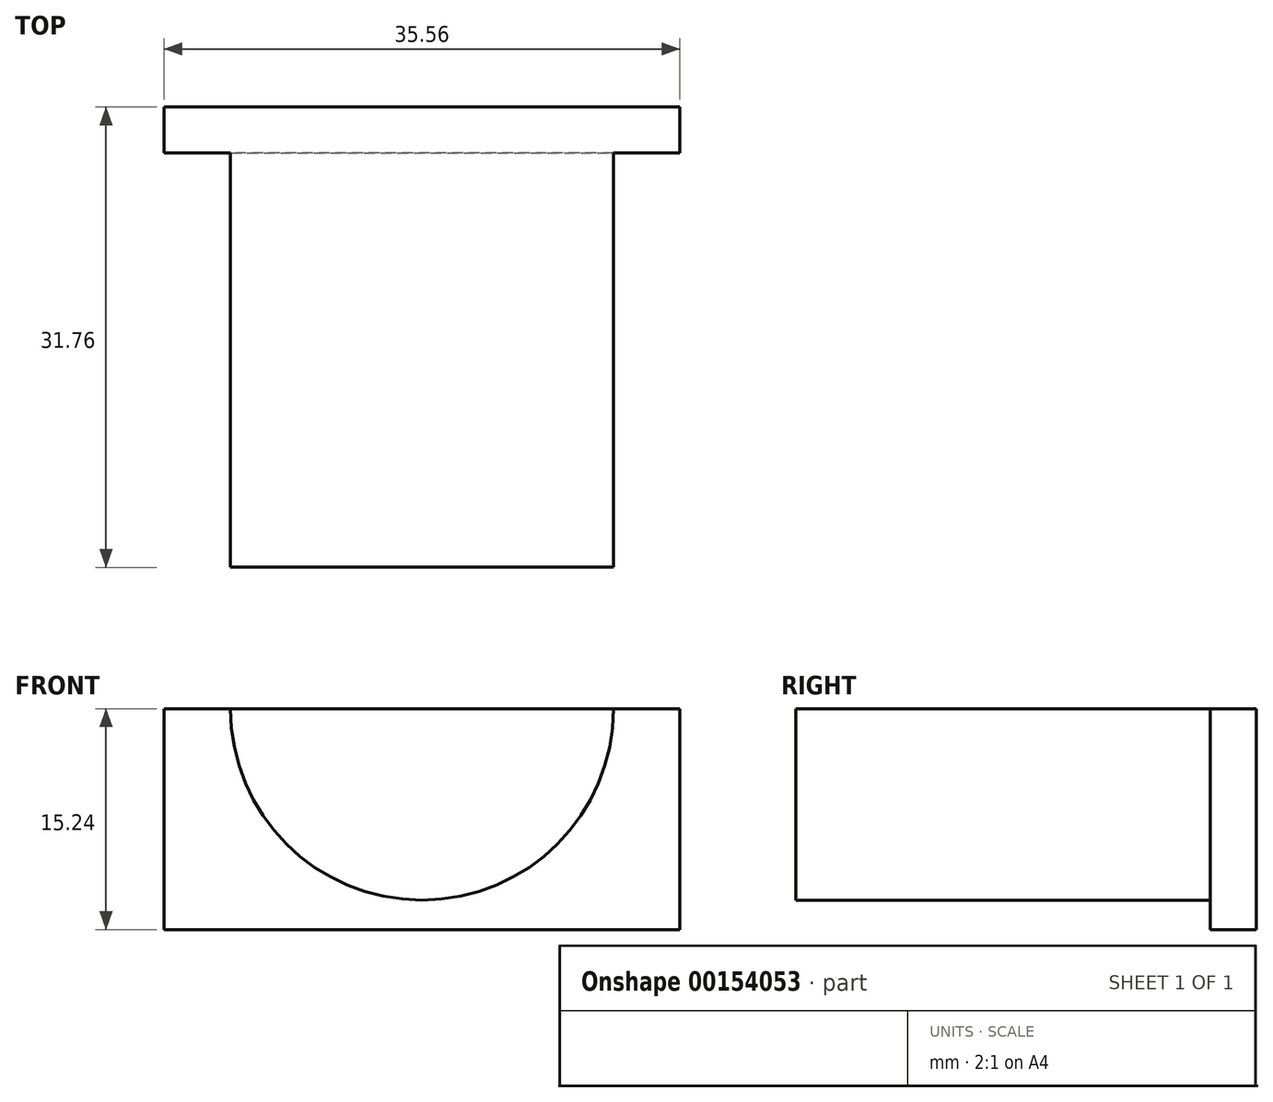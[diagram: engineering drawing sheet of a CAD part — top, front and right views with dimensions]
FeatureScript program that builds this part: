
annotation { "Feature Type Name" : "Feature", "Feature Type Description" : "" }
export const myFeature = defineFeature(function(context is Context, id is Id, definition is map)
    precondition{}
    {
        {
            var Q0;
            Q0=qCreatedBy(makeId("Top.planeOp"),FACE);
            var sketch = newSketch(context, id + "F0", { "sketchPlane" : qUnion([Q0])});
            skLineSegment(sketch, "E0.bottom", {"start": v(17.78, 15.88) * mm, "end": v(-17.78, 15.88) * mm});
            skLineSegment(sketch, "E0.top", {"start": v(17.78, -15.88) * mm, "end": v(-17.78, -15.88) * mm});
            skLineSegment(sketch, "E0.left", {"start": v(17.78, 15.88) * mm, "end": v(17.78, -15.88) * mm});
            skLineSegment(sketch, "E0.right", {"start": v(-17.78, 15.88) * mm, "end": v(-17.78, -15.88) * mm});
            skPoint(sketch, "E0.middle", {"position": v(0, 0) * mm});
            skSolve(sketch);
        }
        {
            var Q0;
            Q0=makeQuery(id+"F0.imprint","IMPRINT",FACE,{"disambiguationData":[TD([[makeQuery(id+"F0.imprint","IMPRINT",EDGE,{"derivedFrom":sQuery(id+"F0.wireOp",EDGE,"E0.bottom")}),1.0]])]});
            extrude(context, id + "F1", {"entities" : qUnion([Q0]), "depth" : 15.24 * mm});
        }
        {
            var Q0;
            Q0=makeQuery(id+"F1.opExtrude","SWEPT_FACE",FACE,{"disambiguationData":[OSD([sQuery(id+"F0.wireOp",EDGE,"E0.top")])]});
            var sketch = newSketch(context, id + "F2", { "sketchPlane" : qUnion([Q0])});
            skArc(sketch, "E1", {"start": v(13.2, 15.24) * mm, "mid": v(0, 2.03) * mm, "end": v(-13.2, 15.24) * mm});
            skSolve(sketch);
        }
        {
            var Q0;
            {var subQ0=sQuery(id+"F2.wireOp",EDGE,"E1");Q0=makeQuery(id+"F2.imprint","IMPRINT",FACE,{"disambiguationData":[TD([[makeQuery(id+"F2.imprint","IMPRINT",EDGE,{"derivedFrom":subQ0}),-1.0]])]});}
            extrude(context, id + "F3", {"entities" : qUnion([Q0]), "operationType" : NewBodyOperationType.REMOVE, "oppositeDirection" : true, "depth" : 28.57 * mm});
        }
    });
